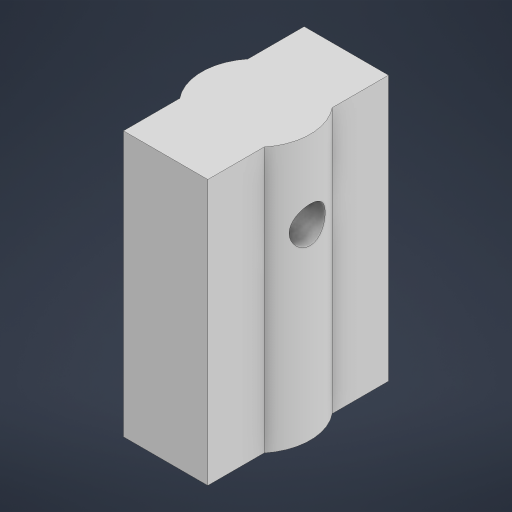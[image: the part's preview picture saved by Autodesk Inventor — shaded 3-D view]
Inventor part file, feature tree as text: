
AUTODESK INVENTOR PART (.ipt)
format: ipt  version: 2023.2 (Build 272271000, 271)  size: 173,056 bytes
history: native  units: mm
features: extrude x2, sketch x2
ambient origin geometry x8: Origin, YZ Plane, XZ Plane, XY Plane, X Axis, Y Axis, Z Axis, Center Point
bodies: Volumenkörper1 (feature_tree)
feature tree (4):
  extrude  "Extrusion1"  Depth=15.0mm
  extrude  "Extrusion2"  Depth=4.5mm TaperAngle=0.0deg
  sketch  "Skizze1"  dims[d0=7.0mm d1=15.0mm]
  sketch  "Skizze2"  dims[d5=4.5mm d6=22.0mm d7=0.0mm d8=3.0mm d9=7.5mm d10=6.5mm d11=0.0mm d12=0.0mm]
